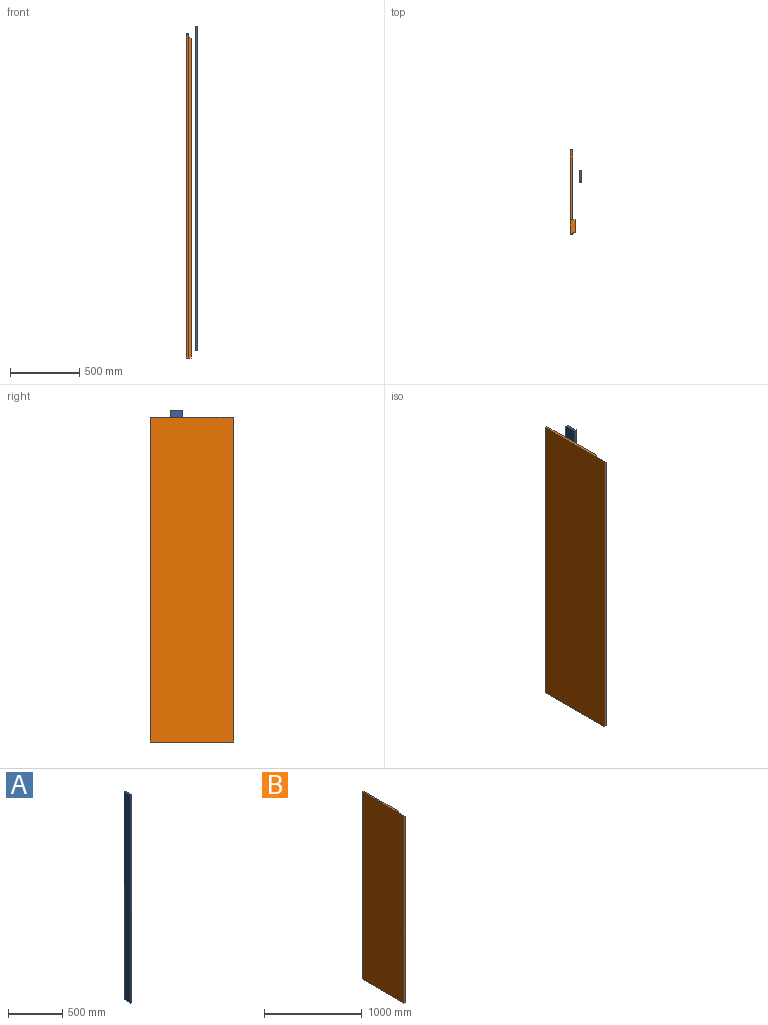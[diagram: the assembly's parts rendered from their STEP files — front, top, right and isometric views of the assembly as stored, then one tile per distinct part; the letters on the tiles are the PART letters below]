
ASSEMBLY  parts=2 mates=1
PART A: 6 faces, bbox 18x85x2350 mm
  f0: plane 85x18mm, normal (0,0,1), area 1530mm2, adj f1,f3,f4,f5
  f1: plane 2350x18mm, normal (0,-1,0), area 42300mm2, adj f0,f2,f4,f5
  f2: plane 85x18mm, normal (0,0,-1), area 1530mm2, adj f1,f3,f4,f5
  f3: plane 2350x18mm, normal (0,1,0), area 42300mm2, adj f0,f2,f4,f5
  f4: plane 2350x85mm, normal (1,0,0), area 199750mm2, adj f0,f1,f2,f3
  f5: plane 2350x85mm, normal (-1,0,0), area 199750mm2, adj f0,f1,f2,f3
PART B: 11 faces, bbox 36x605x2350 mm
  f0: plane 2314x89.61mm, normal (1,0,0), area 207352.2mm2, adj f1,f7,f8,f10
  f1: plane 605x36mm, normal (0,0,-1), area 12596.5mm2, adj f0,f3,f4,f5,f6,f7,f10
  f2: plane 505x18mm, normal (0,0,1), area 9090mm2, adj f4,f5,f6,f9
  f3: plane 2350x18mm, normal (0,-1,0), area 42138mm2, adj f1,f5,f8,f10
  f4: plane 2350x505mm, normal (1,0,0), area 1186750mm2, adj f1,f2,f6,f7,f9
  f5: plane 2350x605mm, normal (-1,0,0), area 1421750mm2, adj f1,f2,f3,f6,f8
  f6: plane 2350x18mm, normal (0,1,0), area 42300mm2, adj f1,f2,f4,f5
  f7: plane 2332x18mm, normal (0,1,0), area 41814mm2, adj f0,f1,f4,f8
  f8: plane 100x36mm, normal (0.71,0,0.71), area 4958.9mm2, adj f0,f3,f5,f7,f9,f10
  f9: plane 18x18mm, normal (0,-1,0), area 162mm2, adj f2,f4,f8
  f10: plane 2332x18mm, normal (0.5,-0.87,0), area 48282.6mm2, adj f0,f1,f3,f8
PLACE A t=(-5216.59,-4530.8,9718.72)mm
PLACE B t=(-5263.86,-4473.49,9665.28)mm
MATE parallel B.f4 <-> A.f5  axis (1,0,0) through (-591.45,-4725.99,-6509.56)mm
